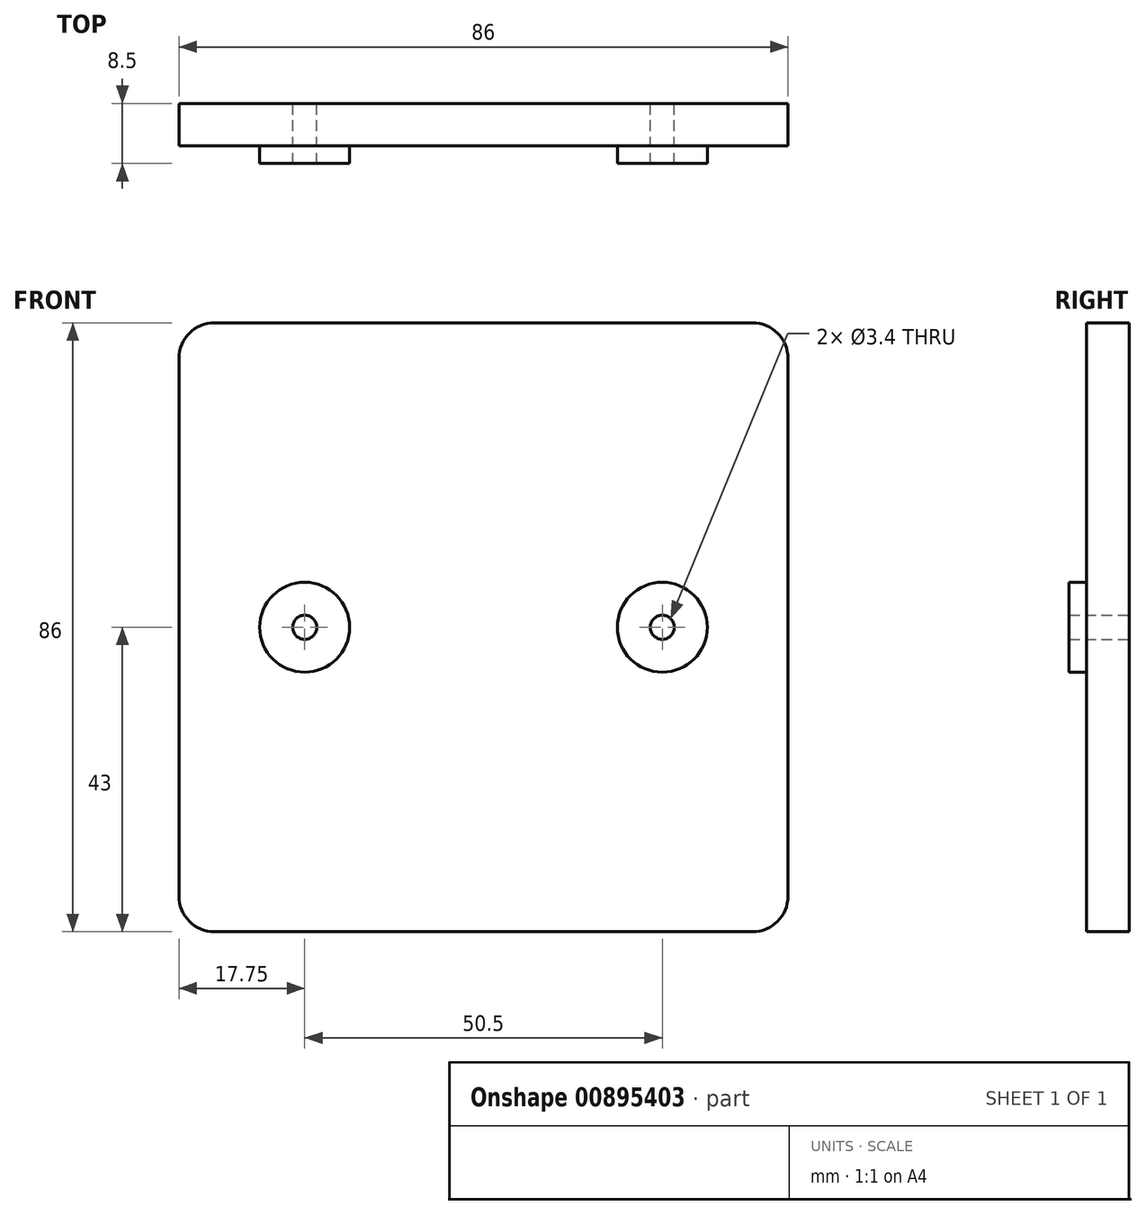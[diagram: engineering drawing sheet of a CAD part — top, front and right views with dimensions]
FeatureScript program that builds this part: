
annotation { "Feature Type Name" : "Feature", "Feature Type Description" : "" }
export const myFeature = defineFeature(function(context is Context, id is Id, definition is map)
    precondition{}
    {
        {
            var Q0;
            Q0=qCreatedBy(makeId("Front.planeOp"),FACE);
            var sketch = newSketch(context, id + "F0", { "sketchPlane" : qUnion([Q0])});
            skLineSegment(sketch, "E0.bottom", {"start": v(-38, 43) * mm, "end": v(38, 43) * mm});
            skLineSegment(sketch, "E0.top", {"start": v(-38, -43) * mm, "end": v(38, -43) * mm});
            skLineSegment(sketch, "E0.left", {"start": v(-43, 38) * mm, "end": v(-43, -38) * mm});
            skLineSegment(sketch, "E0.right", {"start": v(43, 38) * mm, "end": v(43, -38) * mm});
            skPoint(sketch, "E0.middle", {"position": v(0, 0) * mm});
            skPoint(sketch, "E1.visualSharp", {"position": v(-43, 43) * mm});
            skArc(sketch, "E1.filletArc", {"start": v(-38, 43) * mm, "mid": v(-41.54, 41.54) * mm, "end": v(-43, 38) * mm});
            skPoint(sketch, "E2.visualSharp", {"position": v(43, 43) * mm});
            skArc(sketch, "E2.filletArc", {"start": v(43, 38) * mm, "mid": v(41.54, 41.54) * mm, "end": v(38, 43) * mm});
            skPoint(sketch, "E3.visualSharp", {"position": v(43, -43) * mm});
            skArc(sketch, "E3.filletArc", {"start": v(38, -43) * mm, "mid": v(41.54, -41.54) * mm, "end": v(43, -38) * mm});
            skPoint(sketch, "E4.visualSharp", {"position": v(-43, -43) * mm});
            skArc(sketch, "E4.filletArc", {"start": v(-43, -38) * mm, "mid": v(-41.54, -41.54) * mm, "end": v(-38, -43) * mm});
            skLineSegment(sketch, "E5", {"start": v(-25.25, 0) * mm, "end": v(25.25, 0) * mm});
            skCircle(sketch, "E6", {"center": v(-25.25, 0) * mm, "radius": 1.7 * mm});
            skCircle(sketch, "E7", {"center": v(-25.25, 0) * mm, "radius": 6.35 * mm});
            skCircle(sketch, "E8", {"center": v(25.25, 0) * mm, "radius": 1.7 * mm});
            skCircle(sketch, "E9", {"center": v(25.25, 0) * mm, "radius": 6.35 * mm});
            skSolve(sketch);
        }
        {
            var Q0;
            Q0=makeQuery(id+"F0.imprint","IMPRINT",FACE,{"disambiguationData":[TD([[makeQuery(id+"F0.imprint","IMPRINT",EDGE,{"derivedFrom":sQuery(id+"F0.wireOp",EDGE,"E0.bottom")}),-1.0]])]});
            var Q1;
            Q1=makeQuery(id+"F0.imprint","IMPRINT",FACE,{"disambiguationData":[TD([[makeQuery(id+"F0.imprint","IMPRINT",EDGE,{"derivedFrom":sQuery(id+"F0.wireOp",EDGE,"E6")}),-1.0]])]});
            var Q2;
            Q2=makeQuery(id+"F0.imprint","IMPRINT",FACE,{"disambiguationData":[TD([[makeQuery(id+"F0.imprint","IMPRINT",EDGE,{"derivedFrom":sQuery(id+"F0.wireOp",EDGE,"E8")}),-1.0]])]});
            extrude(context, id + "F1", {"entities" : qUnion([Q0, Q1, Q2]), "depth" : 6 * mm, "offsetDistance" : 25 * mm});
        }
        {
            var Q0;
            Q0=makeQuery(id+"F1.opExtrude","CAP_FACE",FACE,{"disambiguationData":[OSD([sQuery(id+"F0.wireOp",EDGE,"E0.bottom"),sQuery(id+"F0.wireOp",EDGE,"E0.top"),sQuery(id+"F0.wireOp",EDGE,"E0.left"),sQuery(id+"F0.wireOp",EDGE,"E0.right"),sQuery(id+"F0.wireOp",EDGE,"E1.filletArc"),sQuery(id+"F0.wireOp",EDGE,"E2.filletArc"),sQuery(id+"F0.wireOp",EDGE,"E3.filletArc"),sQuery(id+"F0.wireOp",EDGE,"E4.filletArc"),sQuery(id+"F0.wireOp",EDGE,"E6"),sQuery(id+"F0.wireOp",EDGE,"E8")])],"isStart":false});
            var sketch = newSketch(context, id + "F2", { "sketchPlane" : qUnion([Q0])});
            skCircle(sketch, "E10", {"center": v(-25.25, 0) * mm, "radius": 6.35 * mm});
            skCircle(sketch, "E11", {"center": v(25.25, 0) * mm, "radius": 6.35 * mm});
            skSolve(sketch);
        }
        {
            var Q0;
            Q0=makeQuery(id+"F2.imprint","IMPRINT",FACE,{"disambiguationData":[TD([[makeQuery(id+"F2.imprint","IMPRINT",EDGE,{"derivedFrom":sQuery(id+"F2.wireOp",EDGE,"E10")}),1.0]])]});
            var Q1;
            Q1=makeQuery(id+"F2.imprint","IMPRINT",FACE,{"disambiguationData":[TD([[makeQuery(id+"F2.imprint","IMPRINT",EDGE,{"derivedFrom":sQuery(id+"F2.wireOp",EDGE,"E11")}),1.0]])]});
            extrude(context, id + "F3", {"entities" : qUnion([Q0, Q1]), "operationType" : NewBodyOperationType.ADD, "depth" : 2.5 * mm, "offsetDistance" : 25 * mm});
        }
    });
